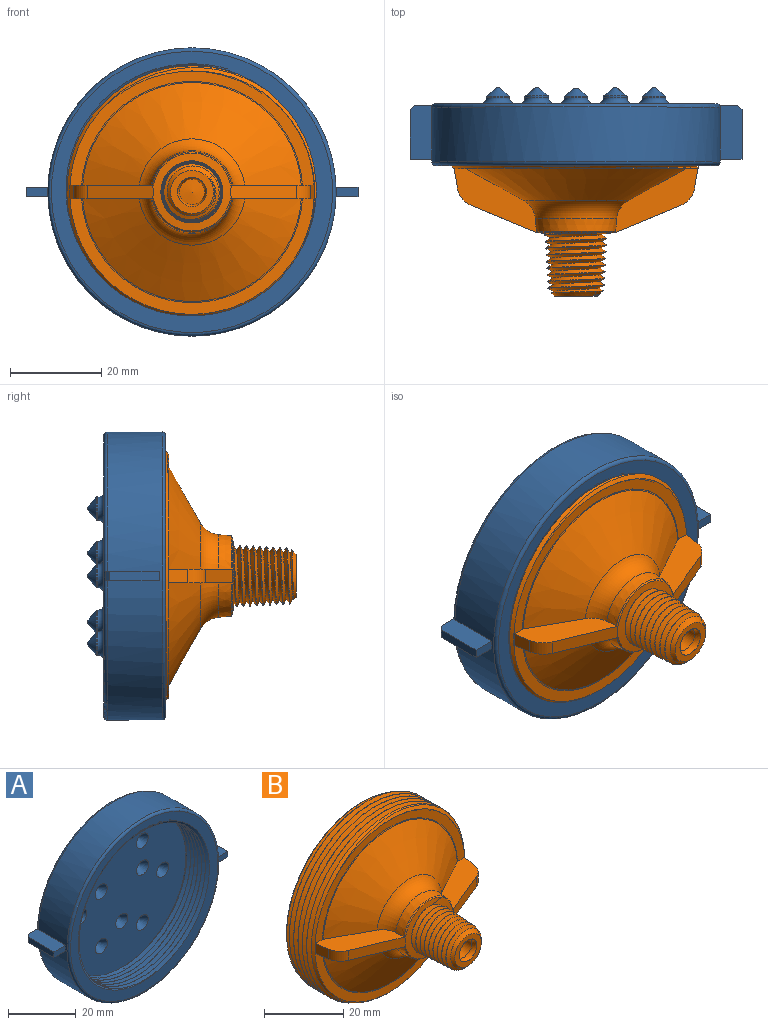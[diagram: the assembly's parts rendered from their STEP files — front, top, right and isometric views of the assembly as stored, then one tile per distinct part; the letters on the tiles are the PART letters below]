
ASSEMBLY  parts=2 mates=1
PART A: 76 faces, bbox 74.2x19.3x69.8 mm
  f0: cylinder r=26.8mm len=53.59mm, axis (0,-1,0), area 148.5mm2, adj f1,f4,f73,f74,f75
  f1: plane 53.59x53.59mm, normal (0,-1,0), area 2073.5mm2, adj f0,f24,f26,f28,f30,f32,f34,f36
  f2: plane 61.67x61.67mm, normal (0,1,0), area 2576.2mm2, adj f54,f55,f56,f57,f58,f59,f60,f61
  f3: cylinder r=31.6mm len=63.19mm, axis (0,-1,0), area 2342.5mm2, adj f41,f42,f43,f46,f47,f50,f53,f54
  f4: plane 63.07x63.07mm, normal (0,-1,0), area 619.6mm2, adj f0,f53,f73,f74
  f5: cylinder r=2.54mm len=5.08mm, axis (0,-1,0), area 6.6mm2, adj f63,f70
  f6: plane 0.61x0.61mm, normal (0,1,0), area 0.1mm2, adj f31,f70
  f7: cylinder r=2.54mm len=5.08mm, axis (0,-1,0), area 6.6mm2, adj f62,f72
  f8: plane 0.61x0.61mm, normal (0,1,0), area 0.1mm2, adj f33,f72
  f9: cylinder r=2.54mm len=5.08mm, axis (0,-1,0), area 6.6mm2, adj f61,f71
  f10: plane 0.61x0.61mm, normal (0,1,0), area 0.1mm2, adj f29,f71
  f11: cylinder r=2.54mm len=5.08mm, axis (0,-1,0), area 6.6mm2, adj f60,f64
  f12: plane 0.61x0.61mm, normal (0,1,0), area 0.1mm2, adj f37,f64
  f13: cylinder r=2.54mm len=5.08mm, axis (0,-1,0), area 6.6mm2, adj f59,f65
  f14: plane 0.61x0.61mm, normal (0,1,0), area 0.1mm2, adj f35,f65
  f15: cylinder r=2.54mm len=5.08mm, axis (0,-1,0), area 6.6mm2, adj f58,f66
  f16: plane 0.61x0.61mm, normal (0,1,0), area 0.1mm2, adj f39,f66
  f17: cylinder r=2.54mm len=5.08mm, axis (0,-1,0), area 6.6mm2, adj f57,f67
  f18: plane 0.61x0.61mm, normal (0,1,0), area 0.1mm2, adj f27,f67
  f19: cylinder r=2.54mm len=5.08mm, axis (0,-1,0), area 6.6mm2, adj f56,f68
  f20: plane 0.61x0.61mm, normal (0,1,0), area 0.1mm2, adj f25,f68
  f21: cylinder r=2.54mm len=5.08mm, axis (0,-1,0), area 6.6mm2, adj f55,f69
  f22: plane 0.61x0.61mm, normal (0,1,0), area 0.1mm2, adj f23,f69
  f23: cylinder r=0.25mm len=4.64mm, axis (0,-1,0), area 7.4mm2, adj f22,f24
  f24: cone r=0.25mm half-angle=37.5deg, axis (0,-1,0), area 33mm2, adj f1,f23
  f25: cylinder r=0.25mm len=4.64mm, axis (0,-1,0), area 7.4mm2, adj f20,f26
  f26: cone r=0.25mm half-angle=37.5deg, axis (0,-1,0), area 33mm2, adj f1,f25
  f27: cylinder r=0.25mm len=4.64mm, axis (0,-1,0), area 7.4mm2, adj f18,f28
  f28: cone r=0.25mm half-angle=37.5deg, axis (0,-1,0), area 33mm2, adj f1,f27
  f29: cylinder r=0.25mm len=4.64mm, axis (0,-1,0), area 7.4mm2, adj f10,f30
  f30: cone r=0.25mm half-angle=37.5deg, axis (0,-1,0), area 33mm2, adj f1,f29
  f31: cylinder r=0.25mm len=4.64mm, axis (0,-1,0), area 7.4mm2, adj f6,f32
  f32: cone r=0.25mm half-angle=37.5deg, axis (0,-1,0), area 33mm2, adj f1,f31
  f33: cylinder r=0.25mm len=4.64mm, axis (0,-1,0), area 7.4mm2, adj f8,f34
  f34: cone r=0.25mm half-angle=37.5deg, axis (0,-1,0), area 33mm2, adj f1,f33
  f35: cylinder r=0.25mm len=4.64mm, axis (0,-1,0), area 7.4mm2, adj f14,f36
  f36: cone r=0.25mm half-angle=37.5deg, axis (0,-1,0), area 33mm2, adj f1,f35
  f37: cylinder r=0.25mm len=4.64mm, axis (0,-1,0), area 7.4mm2, adj f12,f38
  f38: cone r=0.25mm half-angle=37.5deg, axis (0,-1,0), area 33mm2, adj f1,f37
  f39: cylinder r=0.25mm len=4.64mm, axis (0,-1,0), area 7.4mm2, adj f16,f40
  f40: cone r=0.25mm half-angle=37.5deg, axis (0,-1,0), area 33mm2, adj f1,f39
  f41: plane 11.85x4.97mm, normal (0,0,1), area 56.6mm2, adj f3,f43,f44,f45,f51,f54
  f42: plane 11.85x4.97mm, normal (0,0,-1), area 56.6mm2, adj f3,f43,f44,f45,f51,f54
  f43: plane 4.82x2.03mm, normal (0,-1,0), area 9.8mm2, adj f3,f41,f42,f44
  f44: plane 10.83x2.03mm, normal (1,0,0), area 22mm2, adj f41,f42,f43,f51
  f45: plane 3.95x2.03mm, normal (0,1,0), area 8mm2, adj f41,f42,f51,f54
  f46: plane 11.85x4.97mm, normal (0,0,1), area 56.6mm2, adj f3,f48,f49,f50,f52,f54
  f47: plane 11.85x4.97mm, normal (0,0,-1), area 56.6mm2, adj f3,f48,f49,f50,f52,f54
  f48: plane 3.95x2.03mm, normal (0,1,0), area 8mm2, adj f46,f47,f52,f54
  f49: plane 10.83x2.03mm, normal (-1,0,0), area 22mm2, adj f46,f47,f50,f52
  f50: plane 4.82x2.03mm, normal (0,-1,0), area 9.8mm2, adj f3,f46,f47,f49
  f51: plane 2.03x1.02mm, normal (0.71,0.71,0), area 2.9mm2, adj f41,f42,f44,f45
  f52: plane 2.03x1.02mm, normal (-0.71,0.71,0), area 2.9mm2, adj f46,f47,f48,f49
  f53: torus R=30.83mm, axis (0,1,0), area 235.5mm2, adj f3,f4
  f54: torus R=30.83mm, axis (0,-1,0), area 233.6mm2, adj f2,f3,f41,f42,f45,f46,f47,f48
  f55: torus R=3.81mm, axis (0,-1,0), area 37.6mm2, adj f2,f21
  f56: torus R=3.81mm, axis (0,-1,0), area 37.6mm2, adj f2,f19
  f57: torus R=3.81mm, axis (0,-1,0), area 37.6mm2, adj f2,f17
  f58: torus R=3.81mm, axis (0,-1,0), area 37.6mm2, adj f2,f15
  f59: torus R=3.81mm, axis (0,-1,0), area 37.6mm2, adj f2,f13
  f60: torus R=3.81mm, axis (0,-1,0), area 37.6mm2, adj f2,f11
  f61: torus R=3.81mm, axis (0,-1,0), area 37.6mm2, adj f2,f9
  f62: torus R=3.81mm, axis (0,-1,0), area 37.6mm2, adj f2,f7
  f63: torus R=3.81mm, axis (0,-1,0), area 37.6mm2, adj f2,f5
  f64: cone r=2.54mm half-angle=51.5deg, axis (0,-1,0), area 25.5mm2, adj f11,f12
  f65: cone r=2.54mm half-angle=51.5deg, axis (0,-1,0), area 25.5mm2, adj f13,f14
  f66: cone r=2.54mm half-angle=51.5deg, axis (0,-1,0), area 25.5mm2, adj f15,f16
  f67: cone r=2.54mm half-angle=51.5deg, axis (0,-1,0), area 25.5mm2, adj f17,f18
  f68: cone r=2.54mm half-angle=51.5deg, axis (0,-1,0), area 25.5mm2, adj f19,f20
  f69: cone r=2.54mm half-angle=51.5deg, axis (0,-1,0), area 25.5mm2, adj f21,f22
  f70: cone r=2.54mm half-angle=51.5deg, axis (0,-1,0), area 25.5mm2, adj f5,f6
  f71: cone r=2.54mm half-angle=51.5deg, axis (0,-1,0), area 25.5mm2, adj f9,f10
  f72: cone r=2.54mm half-angle=51.5deg, axis (0,-1,0), area 25.5mm2, adj f7,f8
  f73: bspline ~64.93x56.23mm, area 1530.3mm2, adj f0,f4,f74,f75
  f74: bspline ~64.93x56.23mm, area 1400.5mm2, adj f0,f4,f73,f75
  f75: plane 1.52x1.32mm, normal (1,0,0), area 1mm2, adj f0,f73,f74
PART B: 48 faces, bbox 64.7x42.3x56.1 mm
  f0: cone r=27.81mm half-angle=45deg, axis (0,-1,0), area 126.8mm2, adj f1,f27,f28,f29,f30
  f1: cylinder r=27.81mm len=55.63mm, axis (0,1,0), area 33.8mm2, adj f0,f2,f27,f29
  f2: cone r=26.8mm half-angle=45deg, axis (0,1,0), area 96.8mm2, adj f1,f3,f27,f29
  f3: plane 54.08x53.83mm, normal (0,-1,0), area 385.9mm2, adj f2,f4,f20,f21,f22,f23,f24,f25
  f4: torus R=24.26mm, axis (0,-1,0), area 18.7mm2, adj f3,f5,f20,f26
  f5: cone r=24.13mm half-angle=61deg, axis (0,1,0), area 744.9mm2, adj f4,f6,f20,f26
  f6: torus R=14.11mm, axis (0,-1,0), area 141.7mm2, adj f5,f7,f20,f26
  f7: cone r=9.31mm half-angle=4.9deg, axis (0,1,0), area 70.8mm2, adj f6,f8,f20,f26
  f8: cone r=8.54mm half-angle=44.7deg, axis (0,1,0), area 9.4mm2, adj f7,f9,f20,f26
  f9: cone r=8.79mm half-angle=84.6deg, axis (0,1,0), area 230.4mm2, adj f8,f10,f11,f13,f17,f18,f20,f22
  f10: cone r=8.54mm half-angle=44.7deg, axis (0,1,0), area 0mm2, adj f9,f11
  f11: plane 14.47x6.03mm, normal (0.38,-0.92,0), area 47.5mm2, adj f9,f10,f12,f24,f26
  f12: cylinder r=5.08mm len=3.86mm, axis (0,0,-1), area 15.7mm2, adj f11,f24,f25,f26
  f13: cone r=8.54mm half-angle=44.7deg, axis (0,1,0), area 9.4mm2, adj f9,f14,f22,f24
  f14: cone r=9.31mm half-angle=4.9deg, axis (0,1,0), area 70.8mm2, adj f13,f15,f22,f24
  f15: torus R=14.11mm, axis (0,-1,0), area 141.7mm2, adj f14,f16,f22,f24
  f16: cone r=24.13mm half-angle=61deg, axis (0,1,0), area 744.9mm2, adj f15,f22,f23,f24
  f17: cone r=8.54mm half-angle=44.7deg, axis (0,1,0), area 0mm2, adj f9,f18
  f18: plane 14.47x6.03mm, normal (-0.38,-0.92,0), area 47.5mm2, adj f9,f17,f19,f20,f22
  f19: cylinder r=5.08mm len=3.86mm, axis (0,0,-1), area 15.7mm2, adj f18,f20,f21,f22
  f20: plane 18.73x14.45mm, normal (0,0,1), area 111.6mm2, adj f3,f4,f5,f6,f7,f8,f9,f18
  f21: plane 4.2x3.05mm, normal (-0.99,-0.16,0), area 13mm2, adj f3,f19,f20,f22
  f22: plane 18.73x14.45mm, normal (0,0,-1), area 111.6mm2, adj f3,f9,f13,f14,f15,f16,f18,f19
  f23: torus R=24.26mm, axis (0,-1,0), area 18.7mm2, adj f3,f16,f22,f24
  f24: plane 18.73x14.45mm, normal (0,0,-1), area 111.6mm2, adj f3,f9,f11,f12,f13,f14,f15,f16
  f25: plane 4.2x3.05mm, normal (0.99,-0.16,0), area 13mm2, adj f3,f12,f24,f26
  f26: plane 18.73x14.45mm, normal (0,0,1), area 111.6mm2, adj f3,f4,f5,f6,f7,f8,f9,f11
  f27: bspline ~64.23x55.63mm, area 1529.3mm2, adj f0,f1,f2,f3,f28,f29
  f28: plane 0.98x0.93mm, normal (0.77,0,0.63), area 0.2mm2, adj f0,f27,f29
  f29: bspline ~64.23x55.63mm, area 1567.1mm2, adj f0,f1,f2,f3,f27,f28
  f30: plane 53.59x53.59mm, normal (0,1,0), area 228.4mm2, adj f0,f31
  f31: bspline ~50.81x50.81mm, area 707.1mm2, adj f30,f32
  f32: plane 44.89x44.89mm, normal (0,1,0), area 237.3mm2, adj f31,f33
  f33: plane 41.32x41.32mm, normal (0,1,0), area 48.1mm2, adj f32,f34
  f34: cylinder r=20.28mm len=40.56mm, axis (0,-1,0), area 1116.2mm2, adj f33,f35
  f35: plane 40.76x40.76mm, normal (0,-1,0), area 12.4mm2, adj f34,f36
  f36: cone r=22.65mm half-angle=61deg, axis (0,1,0), area 1421.5mm2, adj f35,f37
  f37: torus R=5.31mm, axis (0,1,0), area 64.8mm2, adj f36,f38
  f38: cylinder r=2.77mm len=16.71mm, axis (0,-1,0), area 290.4mm2, adj f37,f39
  f39: torus R=5.31mm, axis (0,-1,0), area 26.7mm2, adj f38,f40
  f40: cylinder r=3.17mm len=6.35mm, axis (0,-1,0), area 0.5mm2, adj f39,f41
  f41: plane 9.44x9.44mm, normal (0,-1,0), area 38.3mm2, adj f40,f42
  f42: cone r=4.72mm half-angle=46.5deg, axis (0,1,0), area 28.8mm2, adj f41,f43,f47
  f43: bspline ~15.33x13.77mm, area 453mm2, adj f42,f44,f45,f46,f47
  f44: cone r=8.79mm half-angle=84.6deg, axis (0,1,0), area 123.5mm2, adj f43,f45,f46
  f45: bspline ~14.35x13.9mm, area 448.1mm2, adj f43,f44,f46,f47
  f46: cone r=6.13mm half-angle=3.1deg, axis (0,1,0), area 26.4mm2, adj f43,f44,f45,f47
  f47: cone r=4.72mm half-angle=46.5deg, axis (0,1,0), area 9.6mm2, adj f42,f43,f45,f46
PLACE A t=(0,42.19,0)mm
PLACE B t=(0,38.1,0)mm
MATE slider B.f0 <-> A.f0  axis (0,1,0) through (0,29.35,0)mm
